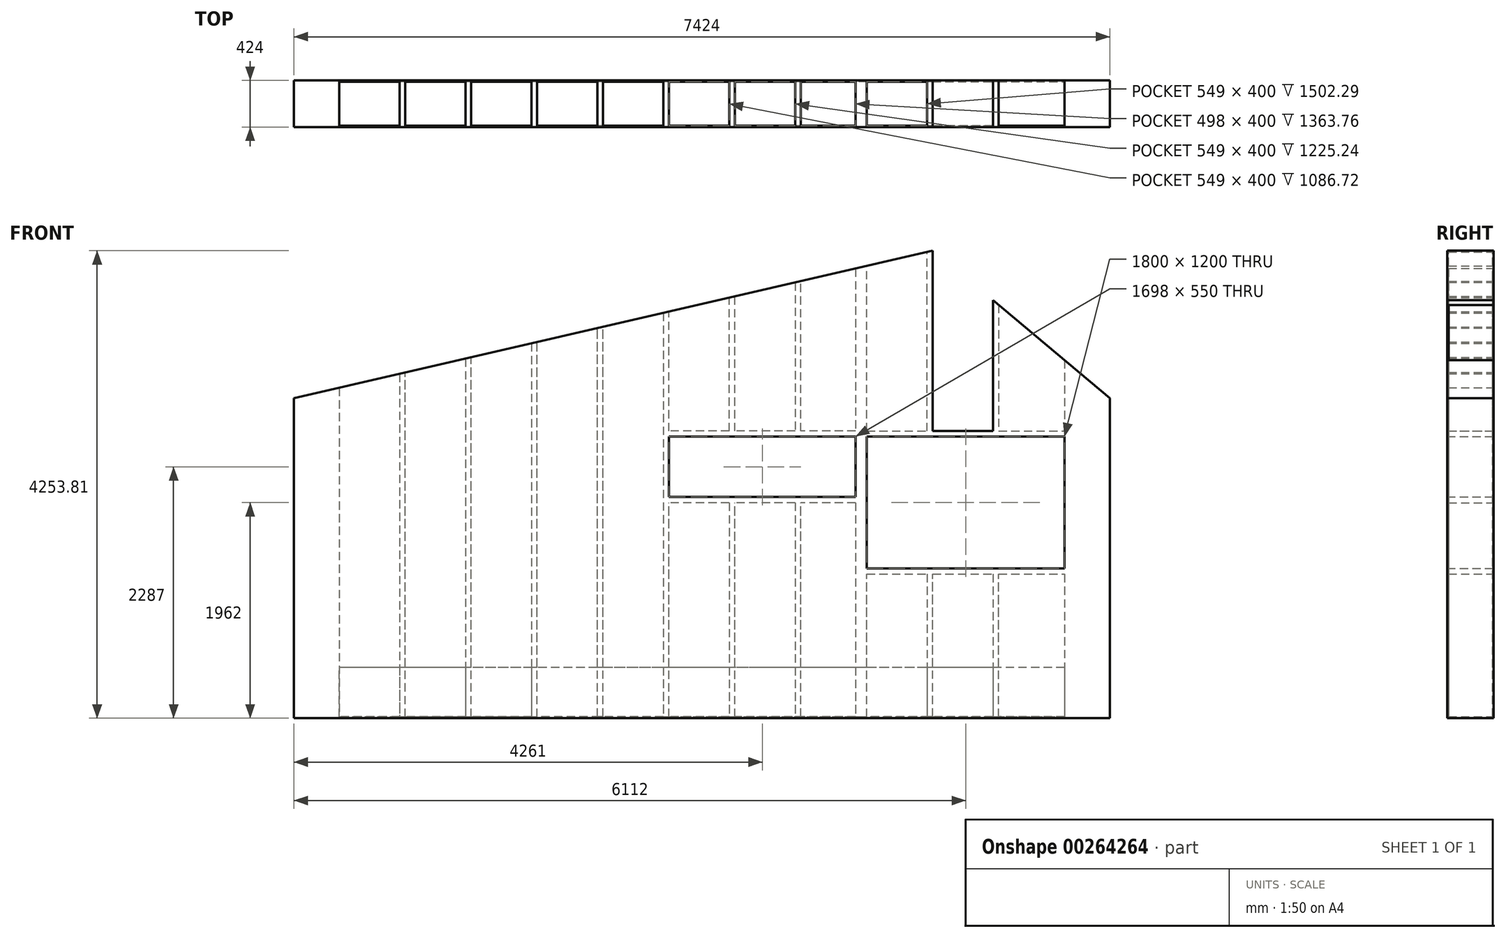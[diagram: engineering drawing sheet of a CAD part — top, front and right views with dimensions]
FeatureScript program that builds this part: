
annotation { "Feature Type Name" : "Feature", "Feature Type Description" : "" }
export const myFeature = defineFeature(function(context is Context, id is Id, definition is map)
    precondition{}
    {
        {
            var Q0;
            Q0=qCreatedBy(makeId("Front.planeOp"),FACE);
            var sketch = newSketch(context, id + "F0", { "sketchPlane" : qUnion([Q0])});
            skLineSegment(sketch, "E0", {"start": v(0, 0) * mm, "end": v(0, 2900) * mm});
            skLineSegment(sketch, "E1", {"start": v(-7424, 2900) * mm, "end": v(-7424, 0) * mm});
            skLineSegment(sketch, "E2", {"start": v(-7424, 0) * mm, "end": v(0, 0) * mm});
            skLineSegment(sketch, "E3", {"start": v(-7012, 2995.12) * mm, "end": v(-7012, 0) * mm});
            skLineSegment(sketch, "E4", {"start": v(-412, 3245.7) * mm, "end": v(-412, 0) * mm});
            skLineSegment(sketch, "E5", {"start": v(-6463, 3121.86) * mm, "end": v(-6463, 0) * mm});
            skLineSegment(sketch, "E6", {"start": v(-6463, 0) * mm, "end": v(-6412, 0) * mm});
            skLineSegment(sketch, "E7", {"start": v(-6412, 0) * mm, "end": v(-6412, 3133.64) * mm});
            skLineSegment(sketch, "E8.1.0.0", {"start": v(-5863, 3121.86) * mm, "end": v(-5863, 0) * mm});
            skLineSegment(sketch, "E8.1.0.1", {"start": v(-5812, 0) * mm, "end": v(-5812, 3133.64) * mm});
            skLineSegment(sketch, "E8.1.0.2", {"start": v(-5863, 0) * mm, "end": v(-5812, 0) * mm});
            skLineSegment(sketch, "E8.2.0.0", {"start": v(-5263, 3121.86) * mm, "end": v(-5263, 0) * mm});
            skLineSegment(sketch, "E8.2.0.1", {"start": v(-5212, 0) * mm, "end": v(-5212, 3133.64) * mm});
            skLineSegment(sketch, "E8.2.0.2", {"start": v(-5263, 0) * mm, "end": v(-5212, 0) * mm});
            skLineSegment(sketch, "E8.3.0.0", {"start": v(-4663, 3121.86) * mm, "end": v(-4663, 0) * mm});
            skLineSegment(sketch, "E8.3.0.1", {"start": v(-4612, 0) * mm, "end": v(-4612, 3133.64) * mm});
            skLineSegment(sketch, "E8.3.0.2", {"start": v(-4663, 0) * mm, "end": v(-4612, 0) * mm});
            skLineSegment(sketch, "E8.4.0.0", {"start": v(-4063, 3121.86) * mm, "end": v(-4063, 0) * mm});
            skLineSegment(sketch, "E8.4.0.1", {"start": v(-4012, 0) * mm, "end": v(-4012, 3133.64) * mm});
            skLineSegment(sketch, "E8.4.0.2", {"start": v(-4063, 0) * mm, "end": v(-4012, 0) * mm});
            skLineSegment(sketch, "E8.5.0.0", {"start": v(-3463, 3121.86) * mm, "end": v(-3463, 2601) * mm});
            skLineSegment(sketch, "E8.5.0.1", {"start": v(-3412, 0) * mm, "end": v(-3412, 1949) * mm});
            skLineSegment(sketch, "E8.5.0.2", {"start": v(-3463, 0) * mm, "end": v(-3412, 0) * mm});
            skLineSegment(sketch, "E8.6.0.0", {"start": v(-2863, 3121.86) * mm, "end": v(-2863, 2601) * mm});
            skLineSegment(sketch, "E8.6.0.1", {"start": v(-2812, 0) * mm, "end": v(-2812, 1949) * mm});
            skLineSegment(sketch, "E8.6.0.2", {"start": v(-2863, 0) * mm, "end": v(-2812, 0) * mm});
            skLineSegment(sketch, "E8.direction1", {"start": v(-6463, 0) * mm, "end": v(-5863, 0) * mm, "construction": true});
            skLineSegment(sketch, "E9", {"start": v(-5863, 3121.86) * mm, "end": v(-5863, 3260.39) * mm});
            skLineSegment(sketch, "E10", {"start": v(-5812, 3272.16) * mm, "end": v(-5812, 3133.64) * mm});
            skLineSegment(sketch, "E11", {"start": v(-5263, 3121.86) * mm, "end": v(-5263, 3398.9) * mm});
            skLineSegment(sketch, "E12", {"start": v(-5212, 3410.68) * mm, "end": v(-5212, 3133.64) * mm});
            skLineSegment(sketch, "E13", {"start": v(-4663, 3121.86) * mm, "end": v(-4663, 3537.43) * mm});
            skLineSegment(sketch, "E14", {"start": v(-4612, 3549.2) * mm, "end": v(-4612, 3133.64) * mm});
            skLineSegment(sketch, "E15", {"start": v(-4063, 3121.86) * mm, "end": v(-4063, 3675.95) * mm});
            skLineSegment(sketch, "E16", {"start": v(-4012, 3687.72) * mm, "end": v(-4012, 3133.64) * mm});
            skLineSegment(sketch, "E17", {"start": v(-3463, 3121.86) * mm, "end": v(-3463, 3814.47) * mm});
            skLineSegment(sketch, "E18", {"start": v(-3412, 3826.24) * mm, "end": v(-3412, 3133.64) * mm});
            skLineSegment(sketch, "E19", {"start": v(-1012, 1) * mm, "end": v(-1063, 1) * mm});
            skLineSegment(sketch, "E20.0.7.0", {"start": v(-2263, 3121.86) * mm, "end": v(-2263, 0) * mm});
            skLineSegment(sketch, "E20.3.7.0", {"start": v(-2212, 0) * mm, "end": v(-2212, 3133.64) * mm});
            skLineSegment(sketch, "E20.6.7.0", {"start": v(-2263, 0) * mm, "end": v(-2212, 0) * mm});
            skLineSegment(sketch, "E21", {"start": v(-2812, 3133.64) * mm, "end": v(-2812, 3964.76) * mm});
            skLineSegment(sketch, "E22", {"start": v(-2863, 3952.99) * mm, "end": v(-2863, 3121.86) * mm});
            skLineSegment(sketch, "E23", {"start": v(-2212, 3133.64) * mm, "end": v(-2212, 4103.29) * mm});
            skLineSegment(sketch, "E24", {"start": v(-2263, 4091.51) * mm, "end": v(-2263, 3121.86) * mm});
            skLineSegment(sketch, "E25.0.8.0", {"start": v(-1663, 3121.86) * mm, "end": v(-1663, 2601) * mm});
            skLineSegment(sketch, "E25.3.8.0", {"start": v(-1612, 0) * mm, "end": v(-1612, 1299) * mm});
            skLineSegment(sketch, "E25.6.8.0", {"start": v(-1663, 0) * mm, "end": v(-1612, 0) * mm});
            skLineSegment(sketch, "E25.0.9.0", {"start": v(-1063, 3121.86) * mm, "end": v(-1063, 2601) * mm});
            skLineSegment(sketch, "E25.3.9.0", {"start": v(-1012, 0) * mm, "end": v(-1012, 1299) * mm});
            skLineSegment(sketch, "E25.6.9.0", {"start": v(-1063, 0) * mm, "end": v(-1012, 0) * mm});
            skLineSegment(sketch, "E26", {"start": v(-1663, 3121.86) * mm, "end": v(-1663, 4230.03) * mm});
            skLineSegment(sketch, "E27", {"start": v(-1612, 4241.8) * mm, "end": v(-1612, 3133.64) * mm});
            skLineSegment(sketch, "E28", {"start": v(-1063, 3121.86) * mm, "end": v(-1063, 3791.96) * mm});
            skLineSegment(sketch, "E29", {"start": v(-1012, 3749.17) * mm, "end": v(-1012, 3133.64) * mm});
            skLineSegment(sketch, "E30", {"start": v(-7424, 2900) * mm, "end": v(-7012, 2995.12) * mm});
            skLineSegment(sketch, "E31", {"start": v(0, 2900) * mm, "end": v(-412, 3245.7) * mm});
            skLineSegment(sketch, "E32", {"start": v(-412, 3245.7) * mm, "end": v(-1601.89, 4244.14) * mm});
            skLineSegment(sketch, "E33", {"start": v(-7012, 2995.12) * mm, "end": v(-1601.89, 4244.14) * mm});
            skLineSegment(sketch, "E34", {"start": v(-412, 2550) * mm, "end": v(-2212, 2550) * mm});
            skLineSegment(sketch, "E35", {"start": v(-2212, 1350) * mm, "end": v(-412, 1350) * mm});
            skLineSegment(sketch, "E36", {"start": v(-2212, 1299) * mm, "end": v(-412, 1299) * mm});
            skLineSegment(sketch, "E37", {"start": v(-2212, 2601) * mm, "end": v(-412, 2601) * mm});
            skLineSegment(sketch, "E38.trimOffspring", {"start": v(-1612, 1) * mm, "end": v(-2263, 1) * mm});
            skLineSegment(sketch, "E39.trimOffspring", {"start": v(-2812, 1) * mm, "end": v(-2863, 1) * mm});
            skLineSegment(sketch, "E40.trimOffspring", {"start": v(-4612, 1) * mm, "end": v(-4663, 1) * mm});
            skLineSegment(sketch, "E41.trimOffspring", {"start": v(-1612, 2601) * mm, "end": v(-1612, 3133.64) * mm});
            skLineSegment(sketch, "E42.trimOffspring", {"start": v(-1663, 1299) * mm, "end": v(-1663, 0) * mm});
            skLineSegment(sketch, "E43.trimOffspring", {"start": v(-1063, 1299) * mm, "end": v(-1063, 0) * mm});
            skLineSegment(sketch, "E44.trimOffspring", {"start": v(-1012, 2601) * mm, "end": v(-1012, 3133.64) * mm});
            skLineSegment(sketch, "E45", {"start": v(-2314, 4079.74) * mm, "end": v(-2314, 0) * mm});
            skLineSegment(sketch, "E46", {"start": v(-2314, 2601) * mm, "end": v(-4012, 2601) * mm});
            skLineSegment(sketch, "E47", {"start": v(-2314, 2550) * mm, "end": v(-4012, 2550) * mm});
            skLineSegment(sketch, "E48", {"start": v(-2314, 2000) * mm, "end": v(-4012, 2000) * mm});
            skLineSegment(sketch, "E49", {"start": v(-2314, 1949) * mm, "end": v(-4012, 1949) * mm});
            skLineSegment(sketch, "E50.trimOffspring", {"start": v(-2812, 2601) * mm, "end": v(-2812, 3133.64) * mm});
            skLineSegment(sketch, "E51.trimOffspring", {"start": v(-2863, 1949) * mm, "end": v(-2863, 0) * mm});
            skLineSegment(sketch, "E52.trimOffspring", {"start": v(-3412, 2601) * mm, "end": v(-3412, 3133.64) * mm});
            skLineSegment(sketch, "E53.trimOffspring", {"start": v(-3463, 1949) * mm, "end": v(-3463, 0) * mm});
            skSolve(sketch);
        }
        {
            var Q0;
            {var subQ0=sQuery(id+"F0.wireOp",EDGE,"E19");Q0=makeQuery(id+"F0.imprint","IMPRINT",FACE,{"disambiguationData":[TD([[makeQuery(id+"F0.imprint","IMPRINT",EDGE,{"derivedFrom":subQ0}),1.0]])]});}
            var Q1;
            {var subQ0=sQuery(id+"F0.wireOp",EDGE,"E19");Q1=makeQuery(id+"F0.imprint","IMPRINT",FACE,{"disambiguationData":[TD([[makeQuery(id+"F0.imprint","IMPRINT",EDGE,{"derivedFrom":subQ0}),1.0]])]});}
            var Q2;
            {var subQ0=sQuery(id+"F0.wireOp",EDGE,"E19");Q2=makeQuery(id+"F0.imprint","IMPRINT",FACE,{"disambiguationData":[TD([[makeQuery(id+"F0.imprint","IMPRINT",EDGE,{"derivedFrom":subQ0}),1.0]])]});}
            var Q3;
            {var subQ0=sQuery(id+"F0.wireOp",EDGE,"E19");Q3=makeQuery(id+"F0.imprint","IMPRINT",FACE,{"disambiguationData":[TD([[makeQuery(id+"F0.imprint","IMPRINT",EDGE,{"derivedFrom":subQ0}),1.0]])]});}
            var Q4;
            {var subQ0=sQuery(id+"F0.wireOp",EDGE,"E19");Q4=makeQuery(id+"F0.imprint","IMPRINT",FACE,{"disambiguationData":[TD([[makeQuery(id+"F0.imprint","IMPRINT",EDGE,{"derivedFrom":subQ0}),1.0]])]});}
            var Q5;
            {var subQ0=sQuery(id+"F0.wireOp",EDGE,"E19");Q5=makeQuery(id+"F0.imprint","IMPRINT",FACE,{"disambiguationData":[TD([[makeQuery(id+"F0.imprint","IMPRINT",EDGE,{"derivedFrom":subQ0}),1.0]])]});}
            var Q6;
            {var subQ0=sQuery(id+"F0.wireOp",EDGE,"E5");Q6=makeQuery(id+"F0.imprint","IMPRINT",FACE,{"disambiguationData":[TD([[makeQuery(id+"F0.imprint","IMPRINT",EDGE,{"derivedFrom":subQ0}),1.0]])]});}
            var Q7;
            Q7=makeQuery(id+"F0.imprint","IMPRINT",FACE,{"disambiguationData":[TD([[makeQuery(id+"F0.imprint","IMPRINT",EDGE,{"derivedFrom":sQuery(id+"F0.wireOp",EDGE,"E8.1.0.0")}),1.0]])]});
            var Q8;
            Q8=makeQuery(id+"F0.imprint","IMPRINT",FACE,{"disambiguationData":[TD([[makeQuery(id+"F0.imprint","IMPRINT",EDGE,{"derivedFrom":sQuery(id+"F0.wireOp",EDGE,"E8.1.0.0")}),1.0]])]});
            var Q9;
            Q9=makeQuery(id+"F0.imprint","IMPRINT",FACE,{"disambiguationData":[TD([[makeQuery(id+"F0.imprint","IMPRINT",EDGE,{"derivedFrom":sQuery(id+"F0.wireOp",EDGE,"E8.2.0.0")}),1.0]])]});
            var Q10;
            Q10=makeQuery(id+"F0.imprint","IMPRINT",FACE,{"disambiguationData":[TD([[makeQuery(id+"F0.imprint","IMPRINT",EDGE,{"derivedFrom":sQuery(id+"F0.wireOp",EDGE,"E8.2.0.0")}),1.0]])]});
            var Q11;
            {var subQ0=sQuery(id+"F0.wireOp",EDGE,"E13");Q11=makeQuery(id+"F0.imprint","IMPRINT",FACE,{"disambiguationData":[TD([[makeQuery(id+"F0.imprint","IMPRINT",EDGE,{"derivedFrom":subQ0}),-1.0]])]});}
            var Q12;
            {var subQ0=sQuery(id+"F0.wireOp",EDGE,"E8.3.0.2");Q12=makeQuery(id+"F0.imprint","IMPRINT",FACE,{"disambiguationData":[TD([[makeQuery(id+"F0.imprint","IMPRINT",EDGE,{"derivedFrom":subQ0}),1.0]])]});}
            var Q13;
            Q13=makeQuery(id+"F0.imprint","IMPRINT",FACE,{"disambiguationData":[TD([[makeQuery(id+"F0.imprint","IMPRINT",EDGE,{"derivedFrom":sQuery(id+"F0.wireOp",EDGE,"E8.4.0.0")}),1.0]])]});
            var Q14;
            Q14=makeQuery(id+"F0.imprint","IMPRINT",FACE,{"disambiguationData":[TD([[makeQuery(id+"F0.imprint","IMPRINT",EDGE,{"derivedFrom":sQuery(id+"F0.wireOp",EDGE,"E8.4.0.0")}),1.0]])]});
            var Q15;
            Q15=makeQuery(id+"F0.imprint","IMPRINT",FACE,{"disambiguationData":[TD([[makeQuery(id+"F0.imprint","IMPRINT",EDGE,{"derivedFrom":sQuery(id+"F0.wireOp",EDGE,"E8.5.0.0")}),1.0]])]});
            var Q16;
            Q16=makeQuery(id+"F0.imprint","IMPRINT",FACE,{"disambiguationData":[TD([[makeQuery(id+"F0.imprint","IMPRINT",EDGE,{"derivedFrom":sQuery(id+"F0.wireOp",EDGE,"E8.5.0.0")}),1.0]])]});
            var Q17;
            {var subQ0=sQuery(id+"F0.wireOp",EDGE,"E8.6.0.2");Q17=makeQuery(id+"F0.imprint","IMPRINT",FACE,{"disambiguationData":[TD([[makeQuery(id+"F0.imprint","IMPRINT",EDGE,{"derivedFrom":subQ0}),1.0]])]});}
            var Q18;
            {var subQ0=sQuery(id+"F0.wireOp",EDGE,"E8.3.0.2");Q18=makeQuery(id+"F0.imprint","IMPRINT",FACE,{"disambiguationData":[TD([[makeQuery(id+"F0.imprint","IMPRINT",EDGE,{"derivedFrom":subQ0}),1.0]])]});}
            var Q19;
            Q19=makeQuery(id+"F0.imprint","IMPRINT",FACE,{"disambiguationData":[TD([[makeQuery(id+"F0.imprint","IMPRINT",EDGE,{"derivedFrom":sQuery(id+"F0.wireOp",EDGE,"E8.2.0.0")}),1.0]])]});
            var Q20;
            Q20=makeQuery(id+"F0.imprint","IMPRINT",FACE,{"disambiguationData":[TD([[makeQuery(id+"F0.imprint","IMPRINT",EDGE,{"derivedFrom":sQuery(id+"F0.wireOp",EDGE,"E8.1.0.0")}),1.0]])]});
            var Q21;
            Q21=makeQuery(id+"F0.imprint","IMPRINT",FACE,{"disambiguationData":[TD([[makeQuery(id+"F0.imprint","IMPRINT",EDGE,{"derivedFrom":sQuery(id+"F0.wireOp",EDGE,"E8.1.0.0")}),1.0]])]});
            var Q22;
            Q22=makeQuery(id+"F0.imprint","IMPRINT",FACE,{"disambiguationData":[TD([[makeQuery(id+"F0.imprint","IMPRINT",EDGE,{"derivedFrom":sQuery(id+"F0.wireOp",EDGE,"E8.2.0.0")}),1.0]])]});
            var Q23;
            {var subQ0=sQuery(id+"F0.wireOp",EDGE,"E8.3.0.2");Q23=makeQuery(id+"F0.imprint","IMPRINT",FACE,{"disambiguationData":[TD([[makeQuery(id+"F0.imprint","IMPRINT",EDGE,{"derivedFrom":subQ0}),1.0]])]});}
            var Q24;
            {var subQ0=sQuery(id+"F0.wireOp",EDGE,"E8.3.0.2");Q24=makeQuery(id+"F0.imprint","IMPRINT",FACE,{"disambiguationData":[TD([[makeQuery(id+"F0.imprint","IMPRINT",EDGE,{"derivedFrom":subQ0}),1.0]])]});}
            var Q25;
            Q25=makeQuery(id+"F0.imprint","IMPRINT",FACE,{"disambiguationData":[TD([[makeQuery(id+"F0.imprint","IMPRINT",EDGE,{"derivedFrom":sQuery(id+"F0.wireOp",EDGE,"E8.2.0.0")}),1.0]])]});
            var Q26;
            Q26=makeQuery(id+"F0.imprint","IMPRINT",FACE,{"disambiguationData":[TD([[makeQuery(id+"F0.imprint","IMPRINT",EDGE,{"derivedFrom":sQuery(id+"F0.wireOp",EDGE,"E8.1.0.0")}),1.0]])]});
            var Q27;
            {var subQ0=sQuery(id+"F0.wireOp",EDGE,"E19");Q27=makeQuery(id+"F0.imprint","IMPRINT",FACE,{"disambiguationData":[TD([[makeQuery(id+"F0.imprint","IMPRINT",EDGE,{"derivedFrom":subQ0}),1.0]])]});}
            var Q28;
            {var subQ0=sQuery(id+"F0.wireOp",EDGE,"E19");Q28=makeQuery(id+"F0.imprint","IMPRINT",FACE,{"disambiguationData":[TD([[makeQuery(id+"F0.imprint","IMPRINT",EDGE,{"derivedFrom":subQ0}),1.0]])]});}
            var Q29;
            {var subQ1=sQuery(id+"F0.wireOp",EDGE,"E21");Q29=makeQuery(id+"F0.imprint","IMPRINT",FACE,{"disambiguationData":[TD([[makeQuery(id+"F0.imprint","IMPRINT",EDGE,{"derivedFrom":subQ1}),1.0]])]});}
            var Q30;
            {var subQ1=sQuery(id+"F0.wireOp",EDGE,"E23");Q30=makeQuery(id+"F0.imprint","IMPRINT",FACE,{"disambiguationData":[TD([[makeQuery(id+"F0.imprint","IMPRINT",EDGE,{"derivedFrom":subQ1}),1.0]])]});}
            var Q31;
            {var subQ0=sQuery(id+"F0.wireOp",EDGE,"E19");Q31=makeQuery(id+"F0.imprint","IMPRINT",FACE,{"disambiguationData":[TD([[makeQuery(id+"F0.imprint","IMPRINT",EDGE,{"derivedFrom":subQ0}),1.0]])]});}
            var Q32;
            {var subQ0=sQuery(id+"F0.wireOp",EDGE,"E20.6.7.0");Q32=makeQuery(id+"F0.imprint","IMPRINT",FACE,{"disambiguationData":[TD([[makeQuery(id+"F0.imprint","IMPRINT",EDGE,{"derivedFrom":subQ0}),1.0]])]});}
            var Q33;
            {var subQ0=sQuery(id+"F0.wireOp",EDGE,"E8.6.0.2");Q33=makeQuery(id+"F0.imprint","IMPRINT",FACE,{"disambiguationData":[TD([[makeQuery(id+"F0.imprint","IMPRINT",EDGE,{"derivedFrom":subQ0}),1.0]])]});}
            var Q34;
            {var subQ0=sQuery(id+"F0.wireOp",EDGE,"E37");var subQ1=sQuery(id+"F0.wireOp",EDGE,"E8.6.0.0");var subQ2=makeQuery(id+"F0.imprint","INTERSECT",VERTEX,{"derivedFrom":[subQ1,subQ0]});Q34=makeQuery(id+"F0.imprint","IMPRINT",FACE,{"disambiguationData":[TD([[makeQuery(id+"F0.imprint","IMPRINT",EDGE,{"disambiguationData":[TD([[subQ2,-1.0]])],"derivedFrom":subQ1}),1.0]])]});}
            var Q35;
            {var subQ0=sQuery(id+"F0.wireOp",EDGE,"E35");var subQ1=sQuery(id+"F0.wireOp",EDGE,"E8.6.0.0");var subQ2=makeQuery(id+"F0.imprint","INTERSECT",VERTEX,{"derivedFrom":[subQ1,subQ0]});Q35=makeQuery(id+"F0.imprint","IMPRINT",FACE,{"disambiguationData":[TD([[makeQuery(id+"F0.imprint","IMPRINT",EDGE,{"disambiguationData":[TD([[subQ2,-1.0]])],"derivedFrom":subQ1}),1.0]])]});}
            var Q36;
            {var subQ0=sQuery(id+"F0.wireOp",EDGE,"E39.trimOffspring");Q36=makeQuery(id+"F0.imprint","IMPRINT",FACE,{"disambiguationData":[TD([[makeQuery(id+"F0.imprint","IMPRINT",EDGE,{"derivedFrom":subQ0}),-1.0]])]});}
            var Q37;
            Q37=makeQuery(id+"F0.imprint","IMPRINT",FACE,{"disambiguationData":[TD([[makeQuery(id+"F0.imprint","IMPRINT",EDGE,{"derivedFrom":sQuery(id+"F0.wireOp",EDGE,"E8.5.0.0")}),1.0]])]});
            var Q38;
            Q38=makeQuery(id+"F0.imprint","IMPRINT",FACE,{"disambiguationData":[TD([[makeQuery(id+"F0.imprint","IMPRINT",EDGE,{"derivedFrom":sQuery(id+"F0.wireOp",EDGE,"E8.4.0.0")}),1.0]])]});
            var Q39;
            Q39=makeQuery(id+"F0.imprint","IMPRINT",FACE,{"disambiguationData":[TD([[makeQuery(id+"F0.imprint","IMPRINT",EDGE,{"derivedFrom":sQuery(id+"F0.wireOp",EDGE,"E8.4.0.0")}),1.0]])]});
            var Q40;
            Q40=makeQuery(id+"F0.imprint","IMPRINT",FACE,{"disambiguationData":[TD([[makeQuery(id+"F0.imprint","IMPRINT",EDGE,{"derivedFrom":sQuery(id+"F0.wireOp",EDGE,"E8.5.0.0")}),1.0]])]});
            var Q41;
            {var subQ0=sQuery(id+"F0.wireOp",EDGE,"E8.6.0.2");Q41=makeQuery(id+"F0.imprint","IMPRINT",FACE,{"disambiguationData":[TD([[makeQuery(id+"F0.imprint","IMPRINT",EDGE,{"derivedFrom":subQ0}),1.0]])]});}
            var Q42;
            {var subQ0=sQuery(id+"F0.wireOp",EDGE,"E37");var subQ1=sQuery(id+"F0.wireOp",EDGE,"E8.6.0.0");var subQ2=makeQuery(id+"F0.imprint","INTERSECT",VERTEX,{"derivedFrom":[subQ1,subQ0]});Q42=makeQuery(id+"F0.imprint","IMPRINT",FACE,{"disambiguationData":[TD([[makeQuery(id+"F0.imprint","IMPRINT",EDGE,{"disambiguationData":[TD([[subQ2,-1.0]])],"derivedFrom":subQ1}),1.0]])]});}
            var Q43;
            {var subQ0=sQuery(id+"F0.wireOp",EDGE,"E35");var subQ1=sQuery(id+"F0.wireOp",EDGE,"E8.6.0.0");var subQ2=makeQuery(id+"F0.imprint","INTERSECT",VERTEX,{"derivedFrom":[subQ1,subQ0]});Q43=makeQuery(id+"F0.imprint","IMPRINT",FACE,{"disambiguationData":[TD([[makeQuery(id+"F0.imprint","IMPRINT",EDGE,{"disambiguationData":[TD([[subQ2,-1.0]])],"derivedFrom":subQ1}),1.0]])]});}
            var Q44;
            {var subQ0=sQuery(id+"F0.wireOp",EDGE,"E39.trimOffspring");Q44=makeQuery(id+"F0.imprint","IMPRINT",FACE,{"disambiguationData":[TD([[makeQuery(id+"F0.imprint","IMPRINT",EDGE,{"derivedFrom":subQ0}),-1.0]])]});}
            var Q45;
            {var subQ0=sQuery(id+"F0.wireOp",EDGE,"E8.6.0.2");Q45=makeQuery(id+"F0.imprint","IMPRINT",FACE,{"disambiguationData":[TD([[makeQuery(id+"F0.imprint","IMPRINT",EDGE,{"derivedFrom":subQ0}),1.0]])]});}
            var Q46;
            {var subQ0=sQuery(id+"F0.wireOp",EDGE,"E37");var subQ1=sQuery(id+"F0.wireOp",EDGE,"E8.6.0.0");var subQ2=makeQuery(id+"F0.imprint","INTERSECT",VERTEX,{"derivedFrom":[subQ1,subQ0]});Q46=makeQuery(id+"F0.imprint","IMPRINT",FACE,{"disambiguationData":[TD([[makeQuery(id+"F0.imprint","IMPRINT",EDGE,{"disambiguationData":[TD([[subQ2,-1.0]])],"derivedFrom":subQ1}),1.0]])]});}
            var Q47;
            {var subQ0=sQuery(id+"F0.wireOp",EDGE,"E35");var subQ1=sQuery(id+"F0.wireOp",EDGE,"E8.6.0.0");var subQ2=makeQuery(id+"F0.imprint","INTERSECT",VERTEX,{"derivedFrom":[subQ1,subQ0]});Q47=makeQuery(id+"F0.imprint","IMPRINT",FACE,{"disambiguationData":[TD([[makeQuery(id+"F0.imprint","IMPRINT",EDGE,{"disambiguationData":[TD([[subQ2,-1.0]])],"derivedFrom":subQ1}),1.0]])]});}
            var Q48;
            {var subQ0=sQuery(id+"F0.wireOp",EDGE,"E39.trimOffspring");Q48=makeQuery(id+"F0.imprint","IMPRINT",FACE,{"disambiguationData":[TD([[makeQuery(id+"F0.imprint","IMPRINT",EDGE,{"derivedFrom":subQ0}),-1.0]])]});}
            var Q49;
            Q49=makeQuery(id+"F0.imprint","IMPRINT",FACE,{"disambiguationData":[TD([[makeQuery(id+"F0.imprint","IMPRINT",EDGE,{"derivedFrom":sQuery(id+"F0.wireOp",EDGE,"E8.5.0.0")}),1.0]])]});
            var Q50;
            Q50=makeQuery(id+"F0.imprint","IMPRINT",FACE,{"disambiguationData":[TD([[makeQuery(id+"F0.imprint","IMPRINT",EDGE,{"derivedFrom":sQuery(id+"F0.wireOp",EDGE,"E8.4.0.0")}),1.0]])]});
            var Q51;
            {var subQ3=sQuery(id+"F0.wireOp",EDGE,"E26");Q51=makeQuery(id+"F0.imprint","IMPRINT",FACE,{"disambiguationData":[TD([[makeQuery(id+"F0.imprint","IMPRINT",EDGE,{"derivedFrom":subQ3}),-1.0]])]});}
            var Q52;
            {var subQ2=sQuery(id+"F0.wireOp",EDGE,"E19");Q52=makeQuery(id+"F0.imprint","IMPRINT",FACE,{"disambiguationData":[TD([[makeQuery(id+"F0.imprint","IMPRINT",EDGE,{"derivedFrom":subQ2}),-1.0]])]});}
            var Q53;
            {var subQ0=sQuery(id+"F0.wireOp",EDGE,"E19");Q53=makeQuery(id+"F0.imprint","IMPRINT",FACE,{"disambiguationData":[TD([[makeQuery(id+"F0.imprint","IMPRINT",EDGE,{"derivedFrom":subQ0}),1.0]])]});}
            var Q54;
            {var subQ0=sQuery(id+"F0.wireOp",EDGE,"E19");Q54=makeQuery(id+"F0.imprint","IMPRINT",FACE,{"disambiguationData":[TD([[makeQuery(id+"F0.imprint","IMPRINT",EDGE,{"derivedFrom":subQ0}),1.0]])]});}
            var Q55;
            {var subQ0=sQuery(id+"F0.wireOp",EDGE,"E25.6.8.0");Q55=makeQuery(id+"F0.imprint","IMPRINT",FACE,{"disambiguationData":[TD([[makeQuery(id+"F0.imprint","IMPRINT",EDGE,{"derivedFrom":subQ0}),1.0]])]});}
            var Q56;
            {var subQ0=sQuery(id+"F0.wireOp",EDGE,"E19");Q56=makeQuery(id+"F0.imprint","IMPRINT",FACE,{"disambiguationData":[TD([[makeQuery(id+"F0.imprint","IMPRINT",EDGE,{"derivedFrom":subQ0}),1.0]])]});}
            var Q57;
            {var subQ0=sQuery(id+"F0.wireOp",EDGE,"E5");Q57=makeQuery(id+"F0.imprint","IMPRINT",FACE,{"disambiguationData":[TD([[makeQuery(id+"F0.imprint","IMPRINT",EDGE,{"derivedFrom":subQ0}),1.0]])]});}
            var Q58;
            {var subQ0=sQuery(id+"F0.wireOp",EDGE,"E34");var subQ1=sQuery(id+"F0.wireOp",EDGE,"E20.3.7.0");var subQ2=makeQuery(id+"F0.imprint","INTERSECT",VERTEX,{"derivedFrom":[subQ1,subQ0]});Q58=makeQuery(id+"F0.imprint","IMPRINT",FACE,{"disambiguationData":[TD([[makeQuery(id+"F0.imprint","IMPRINT",EDGE,{"disambiguationData":[TD([[subQ2,-1.0]])],"derivedFrom":subQ1}),-1.0]])]});}
            var Q59;
            {var subQ0=sQuery(id+"F0.wireOp",EDGE,"E37");var subQ1=sQuery(id+"F0.wireOp",EDGE,"E20.0.7.0");var subQ2=makeQuery(id+"F0.imprint","INTERSECT",VERTEX,{"derivedFrom":[subQ1,subQ0]});Q59=makeQuery(id+"F0.imprint","IMPRINT",FACE,{"disambiguationData":[TD([[makeQuery(id+"F0.imprint","IMPRINT",EDGE,{"disambiguationData":[TD([[subQ2,-1.0]])],"derivedFrom":subQ1}),1.0]])]});}
            var Q60;
            {var subQ0=sQuery(id+"F0.wireOp",EDGE,"E35");var subQ1=sQuery(id+"F0.wireOp",EDGE,"E20.0.7.0");var subQ2=makeQuery(id+"F0.imprint","INTERSECT",VERTEX,{"derivedFrom":[subQ1,subQ0]});Q60=makeQuery(id+"F0.imprint","IMPRINT",FACE,{"disambiguationData":[TD([[makeQuery(id+"F0.imprint","IMPRINT",EDGE,{"disambiguationData":[TD([[subQ2,-1.0]])],"derivedFrom":subQ1}),1.0]])]});}
            var Q61;
            {var subQ0=sQuery(id+"F0.wireOp",EDGE,"E36");var subQ1=sQuery(id+"F0.wireOp",EDGE,"E20.3.7.0");var subQ2=makeQuery(id+"F0.imprint","INTERSECT",VERTEX,{"derivedFrom":[subQ1,subQ0]});Q61=makeQuery(id+"F0.imprint","IMPRINT",FACE,{"disambiguationData":[TD([[makeQuery(id+"F0.imprint","IMPRINT",EDGE,{"disambiguationData":[TD([[subQ2,-1.0]])],"derivedFrom":subQ1}),-1.0]])]});}
            var Q62;
            {var subQ0=sQuery(id+"F0.wireOp",EDGE,"E38.trimOffspring");var subQ1=sQuery(id+"F0.wireOp",EDGE,"E20.0.7.0");var subQ2=makeQuery(id+"F0.imprint","INTERSECT",VERTEX,{"derivedFrom":[subQ1,subQ0]});Q62=makeQuery(id+"F0.imprint","IMPRINT",FACE,{"disambiguationData":[TD([[makeQuery(id+"F0.imprint","IMPRINT",EDGE,{"disambiguationData":[TD([[subQ2,1.0]])],"derivedFrom":subQ1}),1.0]])]});}
            var Q63;
            {var subQ0=sQuery(id+"F0.wireOp",EDGE,"E36");var subQ1=sQuery(id+"F0.wireOp",EDGE,"E25.0.8.0");var subQ2=makeQuery(id+"F0.imprint","INTERSECT",VERTEX,{"derivedFrom":[subQ1,subQ0]});Q63=makeQuery(id+"F0.imprint","IMPRINT",FACE,{"disambiguationData":[TD([[makeQuery(id+"F0.imprint","IMPRINT",EDGE,{"disambiguationData":[TD([[subQ2,-1.0]])],"derivedFrom":subQ1}),1.0]])]});}
            var Q64;
            {var subQ0=sQuery(id+"F0.wireOp",EDGE,"E35");var subQ1=sQuery(id+"F0.wireOp",EDGE,"E25.0.8.0");var subQ2=makeQuery(id+"F0.imprint","INTERSECT",VERTEX,{"derivedFrom":[subQ1,subQ0]});Q64=makeQuery(id+"F0.imprint","IMPRINT",FACE,{"disambiguationData":[TD([[makeQuery(id+"F0.imprint","IMPRINT",EDGE,{"disambiguationData":[TD([[subQ2,-1.0]])],"derivedFrom":subQ1}),1.0]])]});}
            var Q65;
            {var subQ0=sQuery(id+"F0.wireOp",EDGE,"E36");var subQ1=sQuery(id+"F0.wireOp",EDGE,"E25.3.8.0");var subQ2=makeQuery(id+"F0.imprint","INTERSECT",VERTEX,{"derivedFrom":[subQ1,subQ0]});Q65=makeQuery(id+"F0.imprint","IMPRINT",FACE,{"disambiguationData":[TD([[makeQuery(id+"F0.imprint","IMPRINT",EDGE,{"disambiguationData":[TD([[subQ2,-1.0]])],"derivedFrom":subQ1}),-1.0]])]});}
            var Q66;
            {var subQ0=sQuery(id+"F0.wireOp",EDGE,"E37");var subQ1=sQuery(id+"F0.wireOp",EDGE,"E25.0.8.0");var subQ2=makeQuery(id+"F0.imprint","INTERSECT",VERTEX,{"derivedFrom":[subQ1,subQ0]});Q66=makeQuery(id+"F0.imprint","IMPRINT",FACE,{"disambiguationData":[TD([[makeQuery(id+"F0.imprint","IMPRINT",EDGE,{"disambiguationData":[TD([[subQ2,-1.0]])],"derivedFrom":subQ1}),1.0]])]});}
            var Q67;
            {var subQ6=sQuery(id+"F0.wireOp",EDGE,"E47");Q67=makeQuery(id+"F0.imprint","IMPRINT",FACE,{"disambiguationData":[TD([[makeQuery(id+"F0.imprint","IMPRINT",EDGE,{"derivedFrom":subQ6}),-1.0]])]});}
            var Q68;
            {var subQ4=sQuery(id+"F0.wireOp",EDGE,"E48");Q68=makeQuery(id+"F0.imprint","IMPRINT",FACE,{"disambiguationData":[TD([[makeQuery(id+"F0.imprint","IMPRINT",EDGE,{"derivedFrom":subQ4}),1.0]])]});}
            var Q69;
            {var subQ0=sQuery(id+"F0.wireOp",EDGE,"E24");Q69=makeQuery(id+"F0.imprint","IMPRINT",FACE,{"disambiguationData":[TD([[makeQuery(id+"F0.imprint","IMPRINT",EDGE,{"derivedFrom":subQ0}),-1.0]])]});}
            var Q70;
            {var subQ0=sQuery(id+"F0.wireOp",EDGE,"E36");var subQ1=sQuery(id+"F0.wireOp",EDGE,"E25.3.8.0");var subQ2=makeQuery(id+"F0.imprint","INTERSECT",VERTEX,{"derivedFrom":[subQ1,subQ0]});Q70=makeQuery(id+"F0.imprint","IMPRINT",FACE,{"disambiguationData":[TD([[makeQuery(id+"F0.imprint","IMPRINT",EDGE,{"disambiguationData":[TD([[subQ2,1.0]])],"derivedFrom":subQ1}),1.0]])]});}
            var Q71;
            {var subQ0=sQuery(id+"F0.wireOp",EDGE,"E8.5.0.1");Q71=makeQuery(id+"F0.imprint","IMPRINT",FACE,{"disambiguationData":[TD([[makeQuery(id+"F0.imprint","IMPRINT",EDGE,{"derivedFrom":subQ0}),1.0]])]});}
            var Q72;
            {var subQ3=sQuery(id+"F0.wireOp",EDGE,"E25.0.9.0");Q72=makeQuery(id+"F0.imprint","IMPRINT",FACE,{"disambiguationData":[TD([[makeQuery(id+"F0.imprint","IMPRINT",EDGE,{"derivedFrom":subQ3}),1.0]])]});}
            var Q73;
            {var subQ5=sQuery(id+"F0.wireOp",EDGE,"E0");Q73=makeQuery(id+"F0.imprint","IMPRINT",FACE,{"disambiguationData":[TD([[makeQuery(id+"F0.imprint","IMPRINT",EDGE,{"derivedFrom":subQ5}),1.0]])]});}
            var Q74;
            {var subQ0=sQuery(id+"F0.wireOp",EDGE,"E1");Q74=makeQuery(id+"F0.imprint","IMPRINT",FACE,{"disambiguationData":[TD([[makeQuery(id+"F0.imprint","IMPRINT",EDGE,{"derivedFrom":subQ0}),1.0]])]});}
            extrude(context, id + "F1", {"entities" : qUnion([Q0, Q1, Q2, Q3, Q4, Q5, Q6, Q7, Q8, Q9, Q10, Q11, Q12, Q13, Q14, Q15, Q16, Q17, Q18, Q19, Q20, Q21, Q22, Q23, Q24, Q25, Q26, Q27, Q28, Q29, Q30, Q31, Q32, Q33, Q34, Q35, Q36, Q37, Q38, Q39, Q40, Q41, Q42, Q43, Q44, Q45, Q46, Q47, Q48, Q49, Q50, Q51, Q52, Q53, Q54, Q55, Q56, Q57, Q58, Q59, Q60, Q61, Q62, Q63, Q64, Q65, Q66, Q67, Q68, Q69, Q70, Q71, Q72, Q73, Q74]), "depth" : 400 * mm, "offsetDistance" : 25 * mm});
        }
        {
            var Q0;
            Q0=makeQuery(id+"F1.opExtrude","CAP_FACE",FACE,{"disambiguationData":[OSD([sQuery(id+"F0.wireOp",EDGE,"E0"),sQuery(id+"F0.wireOp",EDGE,"E2"),sQuery(id+"F0.wireOp",EDGE,"E4"),sQuery(id+"F0.wireOp",EDGE,"E8.4.0.0"),sQuery(id+"F0.wireOp",EDGE,"E8.4.0.1"),sQuery(id+"F0.wireOp",EDGE,"E8.4.0.2"),sQuery(id+"F0.wireOp",EDGE,"E8.5.0.0"),sQuery(id+"F0.wireOp",EDGE,"E8.5.0.1"),sQuery(id+"F0.wireOp",EDGE,"E8.5.0.2"),sQuery(id+"F0.wireOp",EDGE,"E8.6.0.0"),sQuery(id+"F0.wireOp",EDGE,"E8.6.0.1"),sQuery(id+"F0.wireOp",EDGE,"E8.6.0.2"),sQuery(id+"F0.wireOp",EDGE,"E15"),sQuery(id+"F0.wireOp",EDGE,"E16"),sQuery(id+"F0.wireOp",EDGE,"E17"),sQuery(id+"F0.wireOp",EDGE,"E18"),sQuery(id+"F0.wireOp",EDGE,"E20.3.7.0"),sQuery(id+"F0.wireOp",EDGE,"E20.6.7.0"),sQuery(id+"F0.wireOp",EDGE,"E21"),sQuery(id+"F0.wireOp",EDGE,"E22"),sQuery(id+"F0.wireOp",EDGE,"E23"),sQuery(id+"F0.wireOp",EDGE,"E25.0.8.0"),sQuery(id+"F0.wireOp",EDGE,"E25.3.8.0"),sQuery(id+"F0.wireOp",EDGE,"E25.6.8.0"),sQuery(id+"F0.wireOp",EDGE,"E25.0.9.0"),sQuery(id+"F0.wireOp",EDGE,"E25.3.9.0"),sQuery(id+"F0.wireOp",EDGE,"E25.6.9.0"),sQuery(id+"F0.wireOp",EDGE,"E26"),sQuery(id+"F0.wireOp",EDGE,"E27"),sQuery(id+"F0.wireOp",EDGE,"E28"),sQuery(id+"F0.wireOp",EDGE,"E29"),sQuery(id+"F0.wireOp",EDGE,"E31"),sQuery(id+"F0.wireOp",EDGE,"E32"),sQuery(id+"F0.wireOp",EDGE,"E33"),sQuery(id+"F0.wireOp",EDGE,"E34"),sQuery(id+"F0.wireOp",EDGE,"E35"),sQuery(id+"F0.wireOp",EDGE,"E36"),sQuery(id+"F0.wireOp",EDGE,"E37"),sQuery(id+"F0.wireOp",EDGE,"E41.trimOffspring"),sQuery(id+"F0.wireOp",EDGE,"E42.trimOffspring"),sQuery(id+"F0.wireOp",EDGE,"E43.trimOffspring"),sQuery(id+"F0.wireOp",EDGE,"E44.trimOffspring"),sQuery(id+"F0.wireOp",EDGE,"E45"),sQuery(id+"F0.wireOp",EDGE,"E46"),sQuery(id+"F0.wireOp",EDGE,"E47"),sQuery(id+"F0.wireOp",EDGE,"E48"),sQuery(id+"F0.wireOp",EDGE,"E49"),sQuery(id+"F0.wireOp",EDGE,"E50.trimOffspring"),sQuery(id+"F0.wireOp",EDGE,"E51.trimOffspring"),sQuery(id+"F0.wireOp",EDGE,"E52.trimOffspring"),sQuery(id+"F0.wireOp",EDGE,"E53.trimOffspring")])],"isStart":false});
            var sketch = newSketch(context, id + "F2", { "sketchPlane" : qUnion([Q0])});
            skLineSegment(sketch, "E54", {"start": v(0, 0) * mm, "end": v(-7424, 0) * mm});
            skLineSegment(sketch, "E55", {"start": v(-7424, 0) * mm, "end": v(-7424, 2900) * mm});
            skLineSegment(sketch, "E56", {"start": v(-7424, 2900) * mm, "end": v(-1601.89, 4244.14) * mm});
            skLineSegment(sketch, "E57", {"start": v(-1601.89, 4244.14) * mm, "end": v(0, 2900) * mm});
            skLineSegment(sketch, "E58", {"start": v(0, 2900) * mm, "end": v(0, 0) * mm});
            skLineSegment(sketch, "E59.bottom", {"start": v(-412, 1350) * mm, "end": v(-2212, 1350) * mm});
            skLineSegment(sketch, "E59.top", {"start": v(-412, 2550) * mm, "end": v(-2212, 2550) * mm});
            skLineSegment(sketch, "E59.left", {"start": v(-412, 1350) * mm, "end": v(-412, 2550) * mm});
            skLineSegment(sketch, "E59.right", {"start": v(-2212, 1350) * mm, "end": v(-2212, 2550) * mm});
            skLineSegment(sketch, "E60.bottom", {"start": v(-2314, 2550) * mm, "end": v(-4012, 2550) * mm});
            skLineSegment(sketch, "E60.top", {"start": v(-2314, 2000) * mm, "end": v(-4012, 2000) * mm});
            skLineSegment(sketch, "E60.left", {"start": v(-2314, 2550) * mm, "end": v(-2314, 2000) * mm});
            skLineSegment(sketch, "E60.right", {"start": v(-4012, 2550) * mm, "end": v(-4012, 2000) * mm});
            skSolve(sketch);
        }
        {
            var Q0;
            {var subQ3=sQuery(id+"F2.wireOp",EDGE,"E57");Q0=makeQuery(id+"F2.imprint","IMPRINT",FACE,{"disambiguationData":[TD([[makeQuery(id+"F2.imprint","IMPRINT",EDGE,{"derivedFrom":subQ3}),-1.0]])]});}
            var Q1;
            {var subQ1=makeQuery(id+"F1.opExtrude","CAP_EDGE",EDGE,{"disambiguationData":[OSD([sQuery(id+"F0.wireOp",EDGE,"E8.3.0.0"),sQuery(id+"F0.wireOp",EDGE,"E13")])],"isStart":false});Q1=makeQuery(id+"F2.imprint","IMPRINT",FACE,{"disambiguationData":[TD([[makeQuery(id+"F2.imprint","IMPRINT",EDGE,{"derivedFrom":subQ1}),-1.0]])]});}
            var Q2;
            {var subQ1=makeQuery(id+"F1.opExtrude","CAP_EDGE",EDGE,{"disambiguationData":[OSD([sQuery(id+"F0.wireOp",EDGE,"E8.2.0.0"),sQuery(id+"F0.wireOp",EDGE,"E11")])],"isStart":false});Q2=makeQuery(id+"F2.imprint","IMPRINT",FACE,{"disambiguationData":[TD([[makeQuery(id+"F2.imprint","IMPRINT",EDGE,{"derivedFrom":subQ1}),1.0]])]});}
            var Q3;
            {var subQ1=makeQuery(id+"F1.opExtrude","CAP_EDGE",EDGE,{"disambiguationData":[OSD([sQuery(id+"F0.wireOp",EDGE,"E8.2.0.1"),sQuery(id+"F0.wireOp",EDGE,"E12")])],"isStart":false});Q3=makeQuery(id+"F2.imprint","IMPRINT",FACE,{"disambiguationData":[TD([[makeQuery(id+"F2.imprint","IMPRINT",EDGE,{"derivedFrom":subQ1}),-1.0]])]});}
            var Q4;
            {var subQ1=makeQuery(id+"F1.opExtrude","CAP_EDGE",EDGE,{"disambiguationData":[OSD([sQuery(id+"F0.wireOp",EDGE,"E8.1.0.1"),sQuery(id+"F0.wireOp",EDGE,"E10")])],"isStart":false});Q4=makeQuery(id+"F2.imprint","IMPRINT",FACE,{"disambiguationData":[TD([[makeQuery(id+"F2.imprint","IMPRINT",EDGE,{"derivedFrom":subQ1}),-1.0]])]});}
            var Q5;
            {var subQ1=makeQuery(id+"F1.opExtrude","CAP_EDGE",EDGE,{"disambiguationData":[OSD([sQuery(id+"F0.wireOp",EDGE,"E8.1.0.0"),sQuery(id+"F0.wireOp",EDGE,"E9")])],"isStart":false});Q5=makeQuery(id+"F2.imprint","IMPRINT",FACE,{"disambiguationData":[TD([[makeQuery(id+"F2.imprint","IMPRINT",EDGE,{"derivedFrom":subQ1}),-1.0]])]});}
            var Q6;
            {var subQ2=sQuery(id+"F2.wireOp",EDGE,"E55");Q6=makeQuery(id+"F2.imprint","IMPRINT",FACE,{"disambiguationData":[TD([[makeQuery(id+"F2.imprint","IMPRINT",EDGE,{"derivedFrom":subQ2}),-1.0]])]});}
            var Q7;
            Q7=makeQuery(id+"F2.imprint","IMPRINT",FACE,{"disambiguationData":[TD([[makeQuery(id+"F2.imprint","IMPRINT",EDGE,{"derivedFrom":sQuery(id+"F2.wireOp",EDGE,"E55")}),1.0]])]});
            var Q8;
            {var subQ0=sQuery(id+"F0.wireOp",EDGE,"E25.0.9.0");var subQ1=makeQuery(id+"F1.opExtrude","CAP_EDGE",EDGE,{"disambiguationData":[OSD([subQ0,sQuery(id+"F0.wireOp",EDGE,"E28")])],"isStart":false});Q8=makeQuery(id+"F2.imprint","IMPRINT",FACE,{"disambiguationData":[TD([[makeQuery(id+"F2.imprint","IMPRINT",EDGE,{"derivedFrom":subQ1}),-1.0]])]});}
            var Q9;
            {var subQ1=sQuery(id+"F0.wireOp",EDGE,"E20.3.7.0");var subQ2=makeQuery(id+"F1.opExtrude","CAP_EDGE",EDGE,{"disambiguationData":[OSD([subQ1,sQuery(id+"F0.wireOp",EDGE,"E23")])],"isStart":false});Q9=makeQuery(id+"F2.imprint","IMPRINT",FACE,{"disambiguationData":[TD([[makeQuery(id+"F2.imprint","IMPRINT",EDGE,{"derivedFrom":subQ2}),-1.0]])]});}
            var Q10;
            {var subQ1=sQuery(id+"F0.wireOp",EDGE,"E50.trimOffspring");var subQ2=makeQuery(id+"F1.opExtrude","CAP_EDGE",EDGE,{"disambiguationData":[OSD([sQuery(id+"F0.wireOp",EDGE,"E21"),subQ1])],"isStart":false});Q10=makeQuery(id+"F2.imprint","IMPRINT",FACE,{"disambiguationData":[TD([[makeQuery(id+"F2.imprint","IMPRINT",EDGE,{"derivedFrom":subQ2}),-1.0]])]});}
            var Q11;
            {var subQ3=sQuery(id+"F0.wireOp",EDGE,"E8.6.0.0");var subQ4=makeQuery(id+"F1.opExtrude","CAP_EDGE",EDGE,{"disambiguationData":[OSD([subQ3,sQuery(id+"F0.wireOp",EDGE,"E22")])],"isStart":false});Q11=makeQuery(id+"F2.imprint","IMPRINT",FACE,{"disambiguationData":[TD([[makeQuery(id+"F2.imprint","IMPRINT",EDGE,{"derivedFrom":subQ4}),-1.0]])]});}
            var Q12;
            {var subQ1=sQuery(id+"F0.wireOp",EDGE,"E8.4.0.1");var subQ2=makeQuery(id+"F1.opExtrude","CAP_EDGE",EDGE,{"disambiguationData":[OSD([subQ1,sQuery(id+"F0.wireOp",EDGE,"E16")])],"isStart":false});Q12=makeQuery(id+"F2.imprint","IMPRINT",FACE,{"disambiguationData":[TD([[makeQuery(id+"F2.imprint","IMPRINT",EDGE,{"derivedFrom":subQ2}),-1.0]])]});}
            var Q13;
            {var subQ5=sQuery(id+"F0.wireOp",EDGE,"E53.trimOffspring");var subQ6=makeQuery(id+"F1.opExtrude","CAP_EDGE",EDGE,{"disambiguationData":[OSD([subQ5])],"isStart":false});Q13=makeQuery(id+"F2.imprint","IMPRINT",FACE,{"disambiguationData":[TD([[makeQuery(id+"F2.imprint","IMPRINT",EDGE,{"derivedFrom":subQ6}),-1.0]])]});}
            var Q14;
            {var subQ1=sQuery(id+"F0.wireOp",EDGE,"E8.5.0.1");var subQ2=makeQuery(id+"F1.opExtrude","CAP_EDGE",EDGE,{"disambiguationData":[OSD([subQ1])],"isStart":false});Q14=makeQuery(id+"F2.imprint","IMPRINT",FACE,{"disambiguationData":[TD([[makeQuery(id+"F2.imprint","IMPRINT",EDGE,{"derivedFrom":subQ2}),-1.0]])]});}
            var Q15;
            {var subQ1=sQuery(id+"F0.wireOp",EDGE,"E8.6.0.1");var subQ2=makeQuery(id+"F1.opExtrude","CAP_EDGE",EDGE,{"disambiguationData":[OSD([subQ1])],"isStart":false});Q15=makeQuery(id+"F2.imprint","IMPRINT",FACE,{"disambiguationData":[TD([[makeQuery(id+"F2.imprint","IMPRINT",EDGE,{"derivedFrom":subQ2}),-1.0]])]});}
            var Q16;
            {var subQ6=sQuery(id+"F0.wireOp",EDGE,"E42.trimOffspring");var subQ7=makeQuery(id+"F1.opExtrude","CAP_EDGE",EDGE,{"disambiguationData":[OSD([subQ6])],"isStart":false});Q16=makeQuery(id+"F2.imprint","IMPRINT",FACE,{"disambiguationData":[TD([[makeQuery(id+"F2.imprint","IMPRINT",EDGE,{"derivedFrom":subQ7}),-1.0]])]});}
            var Q17;
            {var subQ1=sQuery(id+"F0.wireOp",EDGE,"E25.3.8.0");var subQ2=makeQuery(id+"F1.opExtrude","CAP_EDGE",EDGE,{"disambiguationData":[OSD([subQ1])],"isStart":false});Q17=makeQuery(id+"F2.imprint","IMPRINT",FACE,{"disambiguationData":[TD([[makeQuery(id+"F2.imprint","IMPRINT",EDGE,{"derivedFrom":subQ2}),-1.0]])]});}
            var Q18;
            {var subQ5=sQuery(id+"F0.wireOp",EDGE,"E25.3.9.0");var subQ6=makeQuery(id+"F1.opExtrude","CAP_EDGE",EDGE,{"disambiguationData":[OSD([subQ5])],"isStart":false});Q18=makeQuery(id+"F2.imprint","IMPRINT",FACE,{"disambiguationData":[TD([[makeQuery(id+"F2.imprint","IMPRINT",EDGE,{"derivedFrom":subQ6}),-1.0]])]});}
            var Q19;
            {var subQ43=sQuery(id+"F2.wireOp",EDGE,"E58");Q19=makeQuery(id+"F2.imprint","IMPRINT",FACE,{"disambiguationData":[TD([[makeQuery(id+"F2.imprint","IMPRINT",EDGE,{"derivedFrom":subQ43}),1.0]])]});}
            extrude(context, id + "F3", {"entities" : qUnion([Q0, Q1, Q2, Q3, Q4, Q5, Q6, Q7, Q8, Q9, Q10, Q11, Q12, Q13, Q14, Q15, Q16, Q17, Q18, Q19]), "operationType" : NewBodyOperationType.ADD, "depth" : 12 * mm, "offsetDistance" : 25 * mm});
        }
        {
            var Q0;
            Q0=makeQuery(id+"F1.opExtrude","CAP_FACE",FACE,{"disambiguationData":[OSD([sQuery(id+"F0.wireOp",EDGE,"E0"),sQuery(id+"F0.wireOp",EDGE,"E2"),sQuery(id+"F0.wireOp",EDGE,"E4"),sQuery(id+"F0.wireOp",EDGE,"E8.4.0.0"),sQuery(id+"F0.wireOp",EDGE,"E8.4.0.1"),sQuery(id+"F0.wireOp",EDGE,"E8.4.0.2"),sQuery(id+"F0.wireOp",EDGE,"E8.5.0.0"),sQuery(id+"F0.wireOp",EDGE,"E8.5.0.1"),sQuery(id+"F0.wireOp",EDGE,"E8.5.0.2"),sQuery(id+"F0.wireOp",EDGE,"E8.6.0.0"),sQuery(id+"F0.wireOp",EDGE,"E8.6.0.1"),sQuery(id+"F0.wireOp",EDGE,"E8.6.0.2"),sQuery(id+"F0.wireOp",EDGE,"E15"),sQuery(id+"F0.wireOp",EDGE,"E16"),sQuery(id+"F0.wireOp",EDGE,"E17"),sQuery(id+"F0.wireOp",EDGE,"E18"),sQuery(id+"F0.wireOp",EDGE,"E20.3.7.0"),sQuery(id+"F0.wireOp",EDGE,"E20.6.7.0"),sQuery(id+"F0.wireOp",EDGE,"E21"),sQuery(id+"F0.wireOp",EDGE,"E22"),sQuery(id+"F0.wireOp",EDGE,"E23"),sQuery(id+"F0.wireOp",EDGE,"E25.0.8.0"),sQuery(id+"F0.wireOp",EDGE,"E25.3.8.0"),sQuery(id+"F0.wireOp",EDGE,"E25.6.8.0"),sQuery(id+"F0.wireOp",EDGE,"E25.0.9.0"),sQuery(id+"F0.wireOp",EDGE,"E25.3.9.0"),sQuery(id+"F0.wireOp",EDGE,"E25.6.9.0"),sQuery(id+"F0.wireOp",EDGE,"E26"),sQuery(id+"F0.wireOp",EDGE,"E27"),sQuery(id+"F0.wireOp",EDGE,"E28"),sQuery(id+"F0.wireOp",EDGE,"E29"),sQuery(id+"F0.wireOp",EDGE,"E31"),sQuery(id+"F0.wireOp",EDGE,"E32"),sQuery(id+"F0.wireOp",EDGE,"E33"),sQuery(id+"F0.wireOp",EDGE,"E34"),sQuery(id+"F0.wireOp",EDGE,"E35"),sQuery(id+"F0.wireOp",EDGE,"E36"),sQuery(id+"F0.wireOp",EDGE,"E37"),sQuery(id+"F0.wireOp",EDGE,"E41.trimOffspring"),sQuery(id+"F0.wireOp",EDGE,"E42.trimOffspring"),sQuery(id+"F0.wireOp",EDGE,"E43.trimOffspring"),sQuery(id+"F0.wireOp",EDGE,"E44.trimOffspring"),sQuery(id+"F0.wireOp",EDGE,"E45"),sQuery(id+"F0.wireOp",EDGE,"E46"),sQuery(id+"F0.wireOp",EDGE,"E47"),sQuery(id+"F0.wireOp",EDGE,"E48"),sQuery(id+"F0.wireOp",EDGE,"E49"),sQuery(id+"F0.wireOp",EDGE,"E50.trimOffspring"),sQuery(id+"F0.wireOp",EDGE,"E51.trimOffspring"),sQuery(id+"F0.wireOp",EDGE,"E52.trimOffspring"),sQuery(id+"F0.wireOp",EDGE,"E53.trimOffspring")])],"isStart":true});
            var sketch = newSketch(context, id + "F4", { "sketchPlane" : qUnion([Q0])});
            skLineSegment(sketch, "E61", {"start": v(0, 0) * mm, "end": v(0, 2900) * mm});
            skLineSegment(sketch, "E62", {"start": v(0, 2900) * mm, "end": v(1601.89, 4244.14) * mm});
            skLineSegment(sketch, "E63", {"start": v(0, 0) * mm, "end": v(7424, 0) * mm});
            skLineSegment(sketch, "E64", {"start": v(7424, 0) * mm, "end": v(7424, 2900) * mm});
            skLineSegment(sketch, "E65", {"start": v(7424, 2900) * mm, "end": v(1601.89, 4244.14) * mm});
            skLineSegment(sketch, "E66", {"start": v(412, 3245.7) * mm, "end": v(412, 0) * mm});
            skLineSegment(sketch, "E67", {"start": v(7012, 0) * mm, "end": v(7012, 2995.12) * mm});
            skLineSegment(sketch, "E68", {"start": v(412, 450) * mm, "end": v(7012, 450) * mm});
            skLineSegment(sketch, "E69.bottom", {"start": v(412, 1350) * mm, "end": v(2212, 1350) * mm});
            skLineSegment(sketch, "E69.top", {"start": v(412, 2550) * mm, "end": v(2212, 2550) * mm});
            skLineSegment(sketch, "E69.left", {"start": v(412, 1350) * mm, "end": v(412, 2550) * mm});
            skLineSegment(sketch, "E69.right", {"start": v(2212, 1350) * mm, "end": v(2212, 2550) * mm});
            skLineSegment(sketch, "E70.bottom", {"start": v(2314, 2000) * mm, "end": v(4012, 2000) * mm});
            skLineSegment(sketch, "E70.top", {"start": v(2314, 2550) * mm, "end": v(4012, 2550) * mm});
            skLineSegment(sketch, "E70.left", {"start": v(2314, 2000) * mm, "end": v(2314, 2550) * mm});
            skLineSegment(sketch, "E70.right", {"start": v(4012, 2000) * mm, "end": v(4012, 2550) * mm});
            skSolve(sketch);
        }
        {
            var Q0;
            {var subQ0=sQuery(id+"F4.wireOp",EDGE,"E65");var subQ3=sQuery(id+"F4.wireOp",EDGE,"E67");var subQ4=makeQuery(id+"F4.imprint","INTERSECT",VERTEX,{"derivedFrom":[subQ0,subQ3]});Q0=makeQuery(id+"F4.imprint","IMPRINT",FACE,{"disambiguationData":[TD([[makeQuery(id+"F4.imprint","IMPRINT",EDGE,{"disambiguationData":[TD([[subQ4,1.0]])],"derivedFrom":subQ3}),1.0]])]});}
            var Q1;
            Q1=makeQuery(id+"F4.imprint","IMPRINT",FACE,{"disambiguationData":[TD([[makeQuery(id+"F4.imprint","IMPRINT",EDGE,{"derivedFrom":sQuery(id+"F4.wireOp",EDGE,"8JvXnBbT-Hp8Q-h03d-JHrK-HpxFGNcqYe4Q.bottom")}),1.0]])]});
            var Q2;
            {var subQ0=sQuery(id+"F4.wireOp",EDGE,"E65");var subQ1=makeQuery(id+"F1.opExtrude","CAP_EDGE",EDGE,{"disambiguationData":[OSD([sQuery(id+"F0.wireOp",EDGE,"E8.1.0.0"),sQuery(id+"F0.wireOp",EDGE,"E9")])],"isStart":true});var subQ2=makeQuery(id+"F4.imprint","INTERSECT",VERTEX,{"derivedFrom":[subQ1,subQ0]});Q2=makeQuery(id+"F4.imprint","IMPRINT",FACE,{"disambiguationData":[TD([[makeQuery(id+"F4.imprint","IMPRINT",EDGE,{"disambiguationData":[TD([[subQ2,-1.0]])],"derivedFrom":subQ0}),1.0]])]});}
            var Q3;
            {var subQ0=sQuery(id+"F4.wireOp",EDGE,"E65");var subQ1=makeQuery(id+"F1.opExtrude","CAP_EDGE",EDGE,{"disambiguationData":[OSD([sQuery(id+"F0.wireOp",EDGE,"E8.1.0.1"),sQuery(id+"F0.wireOp",EDGE,"E10")])],"isStart":true});var subQ2=makeQuery(id+"F4.imprint","INTERSECT",VERTEX,{"derivedFrom":[subQ1,subQ0]});Q3=makeQuery(id+"F4.imprint","IMPRINT",FACE,{"disambiguationData":[TD([[makeQuery(id+"F4.imprint","IMPRINT",EDGE,{"disambiguationData":[TD([[subQ2,-1.0]])],"derivedFrom":subQ0}),1.0]])]});}
            var Q4;
            {var subQ0=sQuery(id+"F4.wireOp",EDGE,"E65");var subQ1=makeQuery(id+"F1.opExtrude","CAP_EDGE",EDGE,{"disambiguationData":[OSD([sQuery(id+"F0.wireOp",EDGE,"E8.2.0.0"),sQuery(id+"F0.wireOp",EDGE,"E11")])],"isStart":true});var subQ2=makeQuery(id+"F4.imprint","INTERSECT",VERTEX,{"derivedFrom":[subQ1,subQ0]});Q4=makeQuery(id+"F4.imprint","IMPRINT",FACE,{"disambiguationData":[TD([[makeQuery(id+"F4.imprint","IMPRINT",EDGE,{"disambiguationData":[TD([[subQ2,-1.0]])],"derivedFrom":subQ0}),1.0]])]});}
            var Q5;
            {var subQ0=sQuery(id+"F4.wireOp",EDGE,"E65");var subQ1=makeQuery(id+"F1.opExtrude","CAP_EDGE",EDGE,{"disambiguationData":[OSD([sQuery(id+"F0.wireOp",EDGE,"E8.2.0.1"),sQuery(id+"F0.wireOp",EDGE,"E12")])],"isStart":true});var subQ2=makeQuery(id+"F4.imprint","INTERSECT",VERTEX,{"derivedFrom":[subQ1,subQ0]});Q5=makeQuery(id+"F4.imprint","IMPRINT",FACE,{"disambiguationData":[TD([[makeQuery(id+"F4.imprint","IMPRINT",EDGE,{"disambiguationData":[TD([[subQ2,-1.0]])],"derivedFrom":subQ0}),1.0]])]});}
            var Q6;
            {var subQ0=sQuery(id+"F4.wireOp",EDGE,"E65");var subQ1=makeQuery(id+"F1.opExtrude","CAP_EDGE",EDGE,{"disambiguationData":[OSD([sQuery(id+"F0.wireOp",EDGE,"E8.3.0.0"),sQuery(id+"F0.wireOp",EDGE,"E13")])],"isStart":true});var subQ2=makeQuery(id+"F4.imprint","INTERSECT",VERTEX,{"derivedFrom":[subQ1,subQ0]});Q6=makeQuery(id+"F4.imprint","IMPRINT",FACE,{"disambiguationData":[TD([[makeQuery(id+"F4.imprint","IMPRINT",EDGE,{"disambiguationData":[TD([[subQ2,-1.0]])],"derivedFrom":subQ0}),1.0]])]});}
            var Q7;
            {var subQ4=sQuery(id+"F0.wireOp",EDGE,"E13");var subQ7=sQuery(id+"F0.wireOp",EDGE,"E33");var subQ8=makeQuery(id+"F1.opExtrude","CAP_EDGE",EDGE,{"disambiguationData":[OSD([subQ7]),TDD([makeQuery(id+"F0.imprint","IMPRINT",EDGE,{"disambiguationData":[TD([[makeQuery(id+"F0.imprint","INTERSECT",VERTEX,{"derivedFrom":[subQ4,subQ7]}),-1.0]])],"derivedFrom":subQ7})])],"isStart":true});Q7=makeQuery(id+"F4.imprint","IMPRINT",FACE,{"disambiguationData":[TD([[makeQuery(id+"F4.imprint","IMPRINT",EDGE,{"derivedFrom":subQ8}),1.0]])]});}
            var Q8;
            {var subQ4=sQuery(id+"F0.wireOp",EDGE,"E11");var subQ7=sQuery(id+"F0.wireOp",EDGE,"E33");var subQ8=makeQuery(id+"F1.opExtrude","CAP_EDGE",EDGE,{"disambiguationData":[OSD([subQ7]),TDD([makeQuery(id+"F0.imprint","IMPRINT",EDGE,{"disambiguationData":[TD([[makeQuery(id+"F0.imprint","INTERSECT",VERTEX,{"derivedFrom":[subQ4,subQ7]}),-1.0]])],"derivedFrom":subQ7})])],"isStart":true});Q8=makeQuery(id+"F4.imprint","IMPRINT",FACE,{"disambiguationData":[TD([[makeQuery(id+"F4.imprint","IMPRINT",EDGE,{"derivedFrom":subQ8}),1.0]])]});}
            var Q9;
            {var subQ4=sQuery(id+"F0.wireOp",EDGE,"E9");var subQ7=sQuery(id+"F0.wireOp",EDGE,"E33");var subQ8=makeQuery(id+"F1.opExtrude","CAP_EDGE",EDGE,{"disambiguationData":[OSD([subQ7]),TDD([makeQuery(id+"F0.imprint","IMPRINT",EDGE,{"disambiguationData":[TD([[makeQuery(id+"F0.imprint","INTERSECT",VERTEX,{"derivedFrom":[subQ4,subQ7]}),-1.0]])],"derivedFrom":subQ7})])],"isStart":true});Q9=makeQuery(id+"F4.imprint","IMPRINT",FACE,{"disambiguationData":[TD([[makeQuery(id+"F4.imprint","IMPRINT",EDGE,{"derivedFrom":subQ8}),1.0]])]});}
            var Q10;
            {var subQ4=sQuery(id+"F0.wireOp",EDGE,"E8.4.0.1");var subQ5=sQuery(id+"F0.wireOp",EDGE,"E49");var subQ6=makeQuery(id+"F0.imprint","INTERSECT",VERTEX,{"derivedFrom":[subQ4,subQ5]});var subQ9=makeQuery(id+"F1.opExtrude","CAP_EDGE",EDGE,{"disambiguationData":[OSD([subQ5]),TDD([makeQuery(id+"F0.imprint","IMPRINT",EDGE,{"disambiguationData":[TD([[subQ6,1.0]])],"derivedFrom":subQ5})])],"isStart":true});Q10=makeQuery(id+"F4.imprint","IMPRINT",FACE,{"disambiguationData":[TD([[makeQuery(id+"F4.imprint","IMPRINT",EDGE,{"derivedFrom":subQ9}),-1.0]])]});}
            var Q11;
            {var subQ4=sQuery(id+"F0.wireOp",EDGE,"E8.5.0.1");var subQ7=sQuery(id+"F0.wireOp",EDGE,"E49");var subQ8=makeQuery(id+"F1.opExtrude","CAP_EDGE",EDGE,{"disambiguationData":[OSD([subQ7]),TDD([makeQuery(id+"F0.imprint","IMPRINT",EDGE,{"disambiguationData":[TD([[makeQuery(id+"F0.imprint","INTERSECT",VERTEX,{"derivedFrom":[subQ4,subQ7]}),1.0]])],"derivedFrom":subQ7})])],"isStart":true});Q11=makeQuery(id+"F4.imprint","IMPRINT",FACE,{"disambiguationData":[TD([[makeQuery(id+"F4.imprint","IMPRINT",EDGE,{"derivedFrom":subQ8}),-1.0]])]});}
            var Q12;
            {var subQ2=sQuery(id+"F0.wireOp",EDGE,"E49");var subQ6=sQuery(id+"F0.wireOp",EDGE,"E8.6.0.1");var subQ9=makeQuery(id+"F1.opExtrude","CAP_EDGE",EDGE,{"disambiguationData":[OSD([subQ2]),TDD([makeQuery(id+"F0.imprint","IMPRINT",EDGE,{"disambiguationData":[TD([[makeQuery(id+"F0.imprint","INTERSECT",VERTEX,{"derivedFrom":[subQ6,subQ2]}),1.0]])],"derivedFrom":subQ2})])],"isStart":true});Q12=makeQuery(id+"F4.imprint","IMPRINT",FACE,{"disambiguationData":[TD([[makeQuery(id+"F4.imprint","IMPRINT",EDGE,{"derivedFrom":subQ9}),-1.0]])]});}
            var Q13;
            {var subQ4=sQuery(id+"F0.wireOp",EDGE,"E36");var subQ5=sQuery(id+"F0.wireOp",EDGE,"E20.3.7.0");var subQ6=makeQuery(id+"F0.imprint","INTERSECT",VERTEX,{"derivedFrom":[subQ5,subQ4]});var subQ10=makeQuery(id+"F1.opExtrude","CAP_EDGE",EDGE,{"disambiguationData":[OSD([subQ4]),TDD([makeQuery(id+"F0.imprint","IMPRINT",EDGE,{"disambiguationData":[TD([[subQ6,-1.0]])],"derivedFrom":subQ4})])],"isStart":true});Q13=makeQuery(id+"F4.imprint","IMPRINT",FACE,{"disambiguationData":[TD([[makeQuery(id+"F4.imprint","IMPRINT",EDGE,{"derivedFrom":subQ10}),1.0]])]});}
            var Q14;
            {var subQ4=sQuery(id+"F0.wireOp",EDGE,"E25.3.8.0");var subQ7=sQuery(id+"F0.wireOp",EDGE,"E36");var subQ8=makeQuery(id+"F1.opExtrude","CAP_EDGE",EDGE,{"disambiguationData":[OSD([subQ7]),TDD([makeQuery(id+"F0.imprint","IMPRINT",EDGE,{"disambiguationData":[TD([[makeQuery(id+"F0.imprint","INTERSECT",VERTEX,{"derivedFrom":[subQ4,subQ7]}),-1.0]])],"derivedFrom":subQ7})])],"isStart":true});Q14=makeQuery(id+"F4.imprint","IMPRINT",FACE,{"disambiguationData":[TD([[makeQuery(id+"F4.imprint","IMPRINT",EDGE,{"derivedFrom":subQ8}),1.0]])]});}
            var Q15;
            {var subQ1=sQuery(id+"F0.wireOp",EDGE,"E36");var subQ2=sQuery(id+"F0.wireOp",EDGE,"E25.3.9.0");var subQ3=makeQuery(id+"F1.opExtrude","CAP_EDGE",EDGE,{"disambiguationData":[OSD([subQ1]),TDD([makeQuery(id+"F0.imprint","IMPRINT",EDGE,{"disambiguationData":[TD([[makeQuery(id+"F0.imprint","INTERSECT",VERTEX,{"derivedFrom":[subQ2,subQ1]}),-1.0]])],"derivedFrom":subQ1})])],"isStart":true});Q15=makeQuery(id+"F4.imprint","IMPRINT",FACE,{"disambiguationData":[TD([[makeQuery(id+"F4.imprint","IMPRINT",EDGE,{"derivedFrom":subQ3}),1.0]])]});}
            var Q16;
            {var subQ3=sQuery(id+"F0.wireOp",EDGE,"E44.trimOffspring");var subQ4=makeQuery(id+"F1.opExtrude","CAP_EDGE",EDGE,{"disambiguationData":[OSD([sQuery(id+"F0.wireOp",EDGE,"E29"),subQ3])],"isStart":true});Q16=makeQuery(id+"F4.imprint","IMPRINT",FACE,{"disambiguationData":[TD([[makeQuery(id+"F4.imprint","IMPRINT",EDGE,{"derivedFrom":subQ4}),1.0]])]});}
            var Q17;
            {var subQ0=sQuery(id+"F0.wireOp",EDGE,"E25.0.9.0");var subQ1=makeQuery(id+"F1.opExtrude","CAP_EDGE",EDGE,{"disambiguationData":[OSD([subQ0,sQuery(id+"F0.wireOp",EDGE,"E28")])],"isStart":true});Q17=makeQuery(id+"F4.imprint","IMPRINT",FACE,{"disambiguationData":[TD([[makeQuery(id+"F4.imprint","IMPRINT",EDGE,{"derivedFrom":subQ1}),1.0]])]});}
            var Q18;
            {var subQ1=sQuery(id+"F0.wireOp",EDGE,"E20.3.7.0");var subQ2=makeQuery(id+"F1.opExtrude","CAP_EDGE",EDGE,{"disambiguationData":[OSD([subQ1,sQuery(id+"F0.wireOp",EDGE,"E23")])],"isStart":true});Q18=makeQuery(id+"F4.imprint","IMPRINT",FACE,{"disambiguationData":[TD([[makeQuery(id+"F4.imprint","IMPRINT",EDGE,{"derivedFrom":subQ2}),1.0]])]});}
            var Q19;
            {var subQ1=sQuery(id+"F0.wireOp",EDGE,"E50.trimOffspring");var subQ2=makeQuery(id+"F1.opExtrude","CAP_EDGE",EDGE,{"disambiguationData":[OSD([sQuery(id+"F0.wireOp",EDGE,"E21"),subQ1])],"isStart":true});Q19=makeQuery(id+"F4.imprint","IMPRINT",FACE,{"disambiguationData":[TD([[makeQuery(id+"F4.imprint","IMPRINT",EDGE,{"derivedFrom":subQ2}),1.0]])]});}
            var Q20;
            {var subQ3=sQuery(id+"F0.wireOp",EDGE,"E8.6.0.0");var subQ4=makeQuery(id+"F1.opExtrude","CAP_EDGE",EDGE,{"disambiguationData":[OSD([subQ3,sQuery(id+"F0.wireOp",EDGE,"E22")])],"isStart":true});Q20=makeQuery(id+"F4.imprint","IMPRINT",FACE,{"disambiguationData":[TD([[makeQuery(id+"F4.imprint","IMPRINT",EDGE,{"derivedFrom":subQ4}),1.0]])]});}
            var Q21;
            {var subQ1=sQuery(id+"F0.wireOp",EDGE,"E8.4.0.1");var subQ2=makeQuery(id+"F1.opExtrude","CAP_EDGE",EDGE,{"disambiguationData":[OSD([subQ1,sQuery(id+"F0.wireOp",EDGE,"E16")])],"isStart":true});Q21=makeQuery(id+"F4.imprint","IMPRINT",FACE,{"disambiguationData":[TD([[makeQuery(id+"F4.imprint","IMPRINT",EDGE,{"derivedFrom":subQ2}),1.0]])]});}
            var Q22;
            {var subQ6=sQuery(id+"F4.wireOp",EDGE,"E61");Q22=makeQuery(id+"F4.imprint","IMPRINT",FACE,{"disambiguationData":[TD([[makeQuery(id+"F4.imprint","IMPRINT",EDGE,{"derivedFrom":subQ6}),-1.0]])]});}
            var Q23;
            {var subQ5=sQuery(id+"F4.wireOp",EDGE,"E64");Q23=makeQuery(id+"F4.imprint","IMPRINT",FACE,{"disambiguationData":[TD([[makeQuery(id+"F4.imprint","IMPRINT",EDGE,{"derivedFrom":subQ5}),1.0]])]});}
            var Q24;
            Q24 = qSketchRegion(id + "Fxqcjnn5jwHZsnE_1", true);
            extrude(context, id + "F5", {"entities" : qUnion([Q0, Q1, Q2, Q3, Q4, Q5, Q6, Q7, Q8, Q9, Q10, Q11, Q12, Q13, Q14, Q15, Q16, Q17, Q18, Q19, Q20, Q21, Q22, Q23, Q24]), "operationType" : NewBodyOperationType.ADD, "depth" : 12 * mm, "offsetDistance" : 25 * mm});
        }
        {
            var Q0;
            {var subQ0=sQuery(id+"F4.wireOp",EDGE,"E63");var subQ1=sQuery(id+"F0.wireOp",EDGE,"E2");Q0=makeQuery(id+"F5.boolean.opBoolean","MERGE",FACE,{"derivedFrom":[makeQuery(id+"F3.boolean.opBoolean","MERGE",FACE,{"derivedFrom":[makeQuery(id+"F1.opExtrude","SWEPT_FACE",FACE,{"disambiguationData":[OSD([subQ1]),TDD([makeQuery(id+"F0.imprint","IMPRINT",EDGE,{"disambiguationData":[TD([[makeQuery(id+"F0.imprint","INTERSECT",VERTEX,{"derivedFrom":[sQuery(id+"F0.wireOp",EDGE,"E1"),subQ1]}),-1.0]])],"derivedFrom":subQ1})])]}),makeQuery(id+"F1.opExtrude","SWEPT_FACE",FACE,{"disambiguationData":[OSD([subQ1,sQuery(id+"F0.wireOp",EDGE,"E20.6.7.0")])]}),makeQuery(id+"F1.opExtrude","SWEPT_FACE",FACE,{"disambiguationData":[OSD([subQ1]),TDD([makeQuery(id+"F0.imprint","IMPRINT",EDGE,{"disambiguationData":[TD([[makeQuery(id+"F0.imprint","INTERSECT",VERTEX,{"derivedFrom":[sQuery(id+"F0.wireOp",EDGE,"E0"),subQ1]}),1.0]])],"derivedFrom":subQ1})])]}),makeQuery(id+"F1.opExtrude","SWEPT_FACE",FACE,{"disambiguationData":[OSD([sQuery(id+"F0.wireOp",EDGE,"E6")])]}),makeQuery(id+"F1.opExtrude","SWEPT_FACE",FACE,{"disambiguationData":[OSD([sQuery(id+"F0.wireOp",EDGE,"E8.1.0.2")])]}),makeQuery(id+"F1.opExtrude","SWEPT_FACE",FACE,{"disambiguationData":[OSD([sQuery(id+"F0.wireOp",EDGE,"E8.2.0.2")])]}),makeQuery(id+"F1.opExtrude","SWEPT_FACE",FACE,{"disambiguationData":[OSD([sQuery(id+"F0.wireOp",EDGE,"E8.3.0.2")])]}),makeQuery(id+"F1.opExtrude","SWEPT_FACE",FACE,{"disambiguationData":[OSD([sQuery(id+"F0.wireOp",EDGE,"E8.4.0.2")])]}),makeQuery(id+"F1.opExtrude","SWEPT_FACE",FACE,{"disambiguationData":[OSD([sQuery(id+"F0.wireOp",EDGE,"E8.5.0.2")])]}),makeQuery(id+"F1.opExtrude","SWEPT_FACE",FACE,{"disambiguationData":[OSD([sQuery(id+"F0.wireOp",EDGE,"E8.6.0.2")])]}),makeQuery(id+"F1.opExtrude","SWEPT_FACE",FACE,{"disambiguationData":[OSD([sQuery(id+"F0.wireOp",EDGE,"E25.6.8.0")])]}),makeQuery(id+"F1.opExtrude","SWEPT_FACE",FACE,{"disambiguationData":[OSD([sQuery(id+"F0.wireOp",EDGE,"E25.6.9.0")])]}),makeQuery(id+"F3.opExtrude","SWEPT_FACE",FACE,{"disambiguationData":[OSD([sQuery(id+"F2.wireOp",EDGE,"E54")])]})]}),makeQuery(id+"F5.opExtrude","SWEPT_FACE",FACE,{"disambiguationData":[OSD([subQ0]),TDD([makeQuery(id+"F4.imprint","IMPRINT",EDGE,{"disambiguationData":[TD([[makeQuery(id+"F4.imprint","INTERSECT",VERTEX,{"derivedFrom":[sQuery(id+"F4.wireOp",EDGE,"E61"),subQ0]}),1.0],[makeQuery(id+"F4.imprint","INTERSECT",VERTEX,{"derivedFrom":[subQ0,sQuery(id+"F4.wireOp",EDGE,"E66")]}),-1.0]])],"derivedFrom":subQ0})])]}),makeQuery(id+"F5.opExtrude","SWEPT_FACE",FACE,{"disambiguationData":[OSD([subQ0]),TDD([makeQuery(id+"F4.imprint","IMPRINT",EDGE,{"disambiguationData":[TD([[makeQuery(id+"F4.imprint","INTERSECT",VERTEX,{"derivedFrom":[subQ0,sQuery(id+"F4.wireOp",EDGE,"E64")]}),1.0],[makeQuery(id+"F4.imprint","INTERSECT",VERTEX,{"derivedFrom":[subQ0,sQuery(id+"F4.wireOp",EDGE,"E67")]}),-1.0]])],"derivedFrom":subQ0})])]})]});}
            var sketch = newSketch(context, id + "F6", { "sketchPlane" : qUnion([Q0])});
            skLineSegment(sketch, "E71.bottom", {"start": v(0, 412) * mm, "end": v(-7424, 412) * mm});
            skLineSegment(sketch, "E71.top", {"start": v(0, -12) * mm, "end": v(-7424, -12) * mm});
            skLineSegment(sketch, "E71.left", {"start": v(0, 412) * mm, "end": v(0, -12) * mm});
            skLineSegment(sketch, "E71.right", {"start": v(-7424, 412) * mm, "end": v(-7424, -12) * mm});
            skSolve(sketch);
        }
        {
            var Q0;
            Q0 = qSketchRegion(id + "F6", true);
            extrude(context, id + "F7", {"entities" : qUnion([Q0]), "operationType" : NewBodyOperationType.ADD, "depth" : 12 * mm, "offsetDistance" : 25 * mm});
        }
    });
